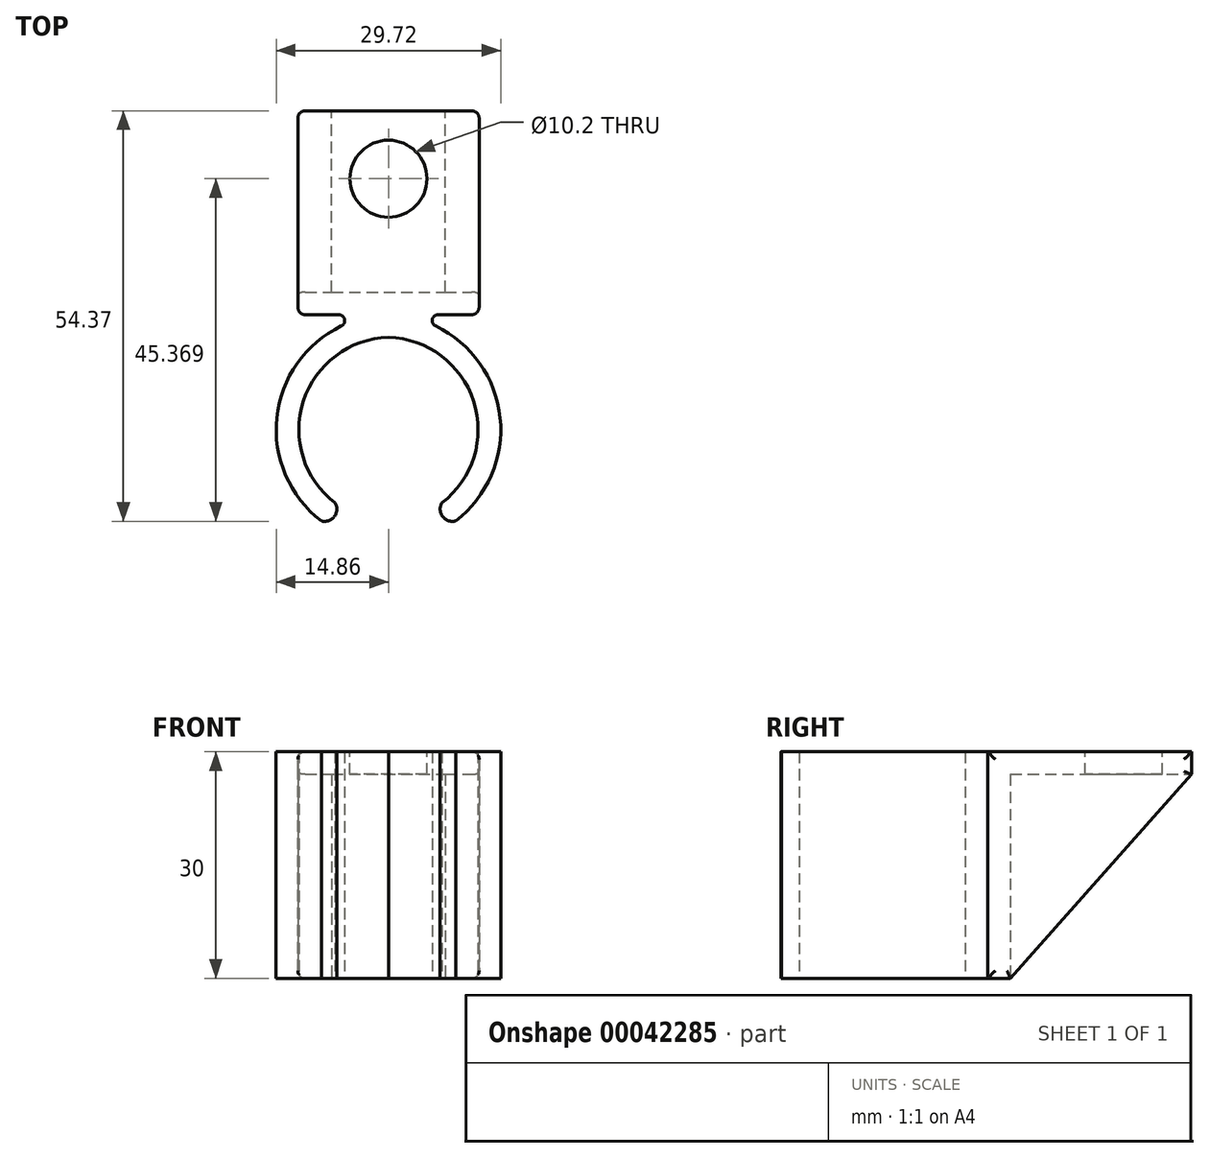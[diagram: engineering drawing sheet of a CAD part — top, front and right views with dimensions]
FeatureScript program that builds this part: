
annotation { "Feature Type Name" : "Feature", "Feature Type Description" : "" }
export const myFeature = defineFeature(function(context is Context, id is Id, definition is map)
    precondition{}
    {
        {
            var Q0;
            Q0=qCreatedBy(makeId("Top.planeOp"),FACE);
            var sketch = newSketch(context, id + "F0", { "sketchPlane" : qUnion([Q0])});
            skCircle(sketch, "E0", {"center": v(0, 0) * mm, "radius": 13.5 * mm, "construction": true});
            skCircle(sketch, "E1", {"center": v(0, 0) * mm, "radius": 11 * mm, "construction": true});
            skLineSegment(sketch, "E2", {"start": v(0, 0) * mm, "end": v(8.68, -10.34) * mm, "construction": true});
            skArc(sketch, "E3", {"start": v(7.07, -8.43) * mm, "mid": v(11.27, 5.03) * mm, "end": v(0, 13.5) * mm});
            skArc(sketch, "E4.0", {"start": v(8.9, -10.8) * mm, "mid": v(14.78, 2.84) * mm, "end": v(6.24, 15) * mm});
            skArc(sketch, "E5", {"start": v(7.07, -8.43) * mm, "mid": v(7.17, -10.24) * mm, "end": v(8.9, -10.8) * mm});
            skArc(sketch, "E6.MirrorCS", {"start": v(-8.9, -10.8) * mm, "mid": v(-14.78, 2.84) * mm, "end": v(-6.24, 15) * mm});
            skArc(sketch, "E7.MirrorCS", {"start": v(-7.07, -8.43) * mm, "mid": v(-11.27, 5.03) * mm, "end": v(0, 13.5) * mm});
            skArc(sketch, "E8.MirrorCS", {"start": v(-7.07, -8.43) * mm, "mid": v(-7.17, -10.24) * mm, "end": v(-8.9, -10.8) * mm});
            skLineSegment(sketch, "E9", {"start": v(6.58, 16.5) * mm, "end": v(12, 16.5) * mm});
            skLineSegment(sketch, "E10", {"start": v(-12, 16.5) * mm, "end": v(-12, 19.5) * mm});
            skLineSegment(sketch, "E11", {"start": v(-12, 19.5) * mm, "end": v(12, 19.5) * mm});
            skLineSegment(sketch, "E12", {"start": v(12, 19.5) * mm, "end": v(12, 16.5) * mm});
            skPoint(sketch, "E13.newPointA", {"position": v(0.09, 16.5) * mm});
            skPoint(sketch, "E13.newPointB", {"position": v(0, 16.5) * mm});
            skArc(sketch, "E13.filletArc", {"start": v(6.58, 16.5) * mm, "mid": v(5.81, 15.89) * mm, "end": v(6.24, 15) * mm});
            skArc(sketch, "E14.MirrorCS", {"start": v(-6.58, 16.5) * mm, "mid": v(-5.81, 15.89) * mm, "end": v(-6.24, 15) * mm});
            skLineSegment(sketch, "E15.trimOffspring", {"start": v(-6.58, 16.5) * mm, "end": v(-12, 16.5) * mm});
            skPoint(sketch, "E16.start.orphan", {"position": v(-0.09, 16.5) * mm});
            skSolve(sketch);
        }
        {
            var Q0;
            Q0 = qSketchRegion(id + "F0", true);
            extrude(context, id + "F1", {"entities" : qUnion([Q0]), "depth" : 30 * mm});
        }
        {
            var Q0;
            Q0=makeQuery(id+"F1.opExtrude","CAP_FACE",FACE,{"disambiguationData":[OSD([sQuery(id+"F0.wireOp",EDGE,"E3"),sQuery(id+"F0.wireOp",EDGE,"E4.0"),sQuery(id+"F0.wireOp",EDGE,"E5"),sQuery(id+"F0.wireOp",EDGE,"E6.MirrorCS"),sQuery(id+"F0.wireOp",EDGE,"E7.MirrorCS"),sQuery(id+"F0.wireOp",EDGE,"E8.MirrorCS"),sQuery(id+"F0.wireOp",EDGE,"E9"),sQuery(id+"F0.wireOp",EDGE,"E10"),sQuery(id+"F0.wireOp",EDGE,"E11"),sQuery(id+"F0.wireOp",EDGE,"E12"),sQuery(id+"F0.wireOp",EDGE,"E13.filletArc"),sQuery(id+"F0.wireOp",EDGE,"E14.MirrorCS"),sQuery(id+"F0.wireOp",EDGE,"E15.trimOffspring")])],"isStart":false});
            var sketch = newSketch(context, id + "F2", { "sketchPlane" : qUnion([Q0])});
            skLineSegment(sketch, "E17.bottom", {"start": v(-12, 19.5) * mm, "end": v(12, 19.5) * mm});
            skLineSegment(sketch, "E17.top", {"start": v(-12, 43.5) * mm, "end": v(12, 43.5) * mm});
            skLineSegment(sketch, "E17.left", {"start": v(-12, 19.5) * mm, "end": v(-12, 43.5) * mm});
            skLineSegment(sketch, "E17.right", {"start": v(12, 19.5) * mm, "end": v(12, 43.5) * mm});
            skCircle(sketch, "E18", {"center": v(0, 34.5) * mm, "radius": 5.1 * mm});
            skSolve(sketch);
        }
        {
            var Q0;
            Q0 = qSketchRegion(id + "F2", true);
            extrude(context, id + "F3", {"entities" : qUnion([Q0]), "oppositeDirection" : true, "depth" : 3 * mm});
        }
        {
            var Q0;
            Q0=makeQuery(id+"F3.opExtrude","SWEPT_BODY",BODY,{"disambiguationData":[OSD([sQuery(id+"F2.wireOp",EDGE,"E17.bottom"),sQuery(id+"F2.wireOp",EDGE,"E17.top"),sQuery(id+"F2.wireOp",EDGE,"E17.left"),sQuery(id+"F2.wireOp",EDGE,"E17.right")])]});
            var Q1;
            Q1=makeQuery(id+"F1.opExtrude","SWEPT_BODY",BODY,{"disambiguationData":[OSD([sQuery(id+"F0.wireOp",EDGE,"E3"),sQuery(id+"F0.wireOp",EDGE,"E4.0"),sQuery(id+"F0.wireOp",EDGE,"E5"),sQuery(id+"F0.wireOp",EDGE,"E6.MirrorCS"),sQuery(id+"F0.wireOp",EDGE,"E7.MirrorCS"),sQuery(id+"F0.wireOp",EDGE,"E8.MirrorCS"),sQuery(id+"F0.wireOp",EDGE,"E9"),sQuery(id+"F0.wireOp",EDGE,"E10"),sQuery(id+"F0.wireOp",EDGE,"E11"),sQuery(id+"F0.wireOp",EDGE,"E12"),sQuery(id+"F0.wireOp",EDGE,"E13.filletArc"),sQuery(id+"F0.wireOp",EDGE,"E14.MirrorCS"),sQuery(id+"F0.wireOp",EDGE,"E15.trimOffspring")])]});
            booleanBodies(context, id + "F4", {"operationType" : BooleanOperationType.UNION, "tools" : qUnion([Q0, Q1])});
        }
        {
            var Q0;
            Q0=makeQuery(id+"F4.opBoolean","MERGE",FACE,{"derivedFrom":[makeQuery(id+"F1.opExtrude","SWEPT_FACE",FACE,{"disambiguationData":[OSD([sQuery(id+"F0.wireOp",EDGE,"E12")])]}),makeQuery(id+"F3.opExtrude","SWEPT_FACE",FACE,{"disambiguationData":[OSD([sQuery(id+"F2.wireOp",EDGE,"E17.right")])]})]});
            var sketch = newSketch(context, id + "F5", { "sketchPlane" : qUnion([Q0])});
            skLineSegment(sketch, "E19", {"start": v(19.5, 0) * mm, "end": v(43.5, 27) * mm});
            skLineSegment(sketch, "E20", {"start": v(43.5, 27) * mm, "end": v(19.5, 27) * mm});
            skLineSegment(sketch, "E21", {"start": v(19.5, 27) * mm, "end": v(19.5, 0) * mm});
            skSolve(sketch);
        }
        {
            var Q0;
            Q0 = qSketchRegion(id + "F5", true);
            extrude(context, id + "F6", {"entities" : qUnion([Q0]), "oppositeDirection" : true, "depth" : 4.5 * mm});
        }
        {
            var Q0;
            Q0=makeQuery(id+"F6.opExtrude","SWEPT_BODY",BODY,{"disambiguationData":[OSD([sQuery(id+"F5.wireOp",EDGE,"E19"),sQuery(id+"F5.wireOp",EDGE,"E20"),sQuery(id+"F5.wireOp",EDGE,"E21")])]});
            var Q1;
            Q1=qCreatedBy(makeId("Right.planeOp"),FACE);
            mirror(context, id + "F7", {"operationType" : NewBodyOperationType.ADD, "entities" : qUnion([Q0]), "mirrorPlane" : qUnion([Q1])});
        }
        {
            var Q0;
            Q0=makeQuery(id+"F7.boolean.opBoolean","MERGE",FACE,{"derivedFrom":[makeQuery(id+"F4.opBoolean","MERGE",FACE,{"derivedFrom":[makeQuery(id+"F1.opExtrude","SWEPT_FACE",FACE,{"disambiguationData":[OSD([sQuery(id+"F0.wireOp",EDGE,"E12")])]}),makeQuery(id+"F3.opExtrude","SWEPT_FACE",FACE,{"disambiguationData":[OSD([sQuery(id+"F2.wireOp",EDGE,"E17.right")])]})]}),makeQuery(id+"F6.opExtrude","CAP_FACE",FACE,{"disambiguationData":[OSD([sQuery(id+"F5.wireOp",EDGE,"E19"),sQuery(id+"F5.wireOp",EDGE,"E20"),sQuery(id+"F5.wireOp",EDGE,"E21")])],"isStart":true})]});
            var Q1;
            Q1=makeQuery(id+"F7.boolean.opBoolean","MERGE",FACE,{"derivedFrom":[makeQuery(id+"F4.opBoolean","MERGE",FACE,{"derivedFrom":[makeQuery(id+"F1.opExtrude","SWEPT_FACE",FACE,{"disambiguationData":[OSD([sQuery(id+"F0.wireOp",EDGE,"E10")])]}),makeQuery(id+"F3.opExtrude","SWEPT_FACE",FACE,{"disambiguationData":[OSD([sQuery(id+"F2.wireOp",EDGE,"E17.left")])]})]}),makeQuery(id+"F7.opPattern","COPY",FACE,{"derivedFrom":makeQuery(id+"F6.opExtrude","CAP_FACE",FACE,{"disambiguationData":[OSD([sQuery(id+"F5.wireOp",EDGE,"E19"),sQuery(id+"F5.wireOp",EDGE,"E20"),sQuery(id+"F5.wireOp",EDGE,"E21")])],"isStart":true}),"instanceName":"1"})]});
            fillet(context, id + "F8", {"entities" : qUnion([Q0, Q1]), "radius" : 1 * mm, "tangentPropagation" : true, "allowEdgeOverflow" : false});
        }
    });
